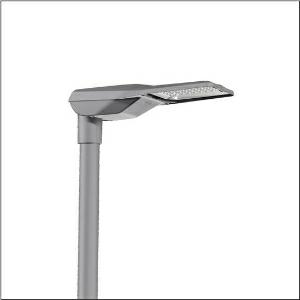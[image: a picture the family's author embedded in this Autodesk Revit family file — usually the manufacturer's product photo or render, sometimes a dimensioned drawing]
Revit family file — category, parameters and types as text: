
# Revit family: streetlight_sl_21_iq_mini___p0_8a_5xe2u31g08gb_20f9
name_source: partatom
category: Lighting Fixtures
units: mm (PartAtom-declared; Revit-internal decimal feet)

## family parameters
Cut with Voids When Loaded = No
Host = Face
Light Source = No
Part Type = Normal
Room Calculation Point = No
Round Connector Dimension = Use Diameter
Shared = No

## types (1)
- --- (1 x LED, 5730 lm, 37.1 W, 3000K)
    Apparent Load = 37 VA
    CIE Flux Codes = 33 69 96 100 100
    Color Rendering = 70
    Color Temperature = 3000K
    Default Elevation = 1800 mm
    Description = Streetlight SL 21 iQ mini, mast luminaire, primary light control with lens, of PMMA, primary optical cover: cover, of toughened safety glass, transparent, light distribution: P0.8a, light emission: direct distribution, primary light characteristic: asymmetric, installation type: post-top, side-entry, LED, High Power LED, rated luminous flux: 5.730lm, luminous efficacy: 154lm/W, light colour: 730, colour temperature: 3000K, control gear: iQ Street-Remote, control: pre-setting: linear dimming characteristic, Street-Remote, Auto-Match, Temp-Guard, Lumen-Switch, Night-Set, Smart-Wire, Light-Fading, Desk-Remote (wireless, voltage-free reading and setting of iQ features in the workshop via application-optimized NFC function/RFID function), optimised constant luminous flux control (CLO 2.0), mains connection: 220..240V, AC, 50/60Hz, start of lifetime: 37W, end of service life: 39W, reduction: 18W, luminaire housing, of diecast aluminium, powder-coated, SITECO metallic grey (DB 702S), corrosivity category C5 high according to DIN EN ISO 12944, please order mast flange separately, inclination adjustable: 0°, 5°, 10°, 15°, sealing non-destructively replaceable, multi-level sealing system, length: 628mm, width: 235mm, height: 110mm, mast flange for spigot size: 42mm (side-entry): 5XC10008XM4, 60/48mm (side-entry/post-top): 5XC10108XM2, 76/60mm (side-entry/post-top): 5XC10108XM1, mounting height: 4..8m, protection rating (complete): IP66, insulation class (complete): insulation class II (safety insulation), certification: CE, ENEC, ENEC+, VDE, impact resistance: IK10, permissible operating ambient temperature for outdoor applications: -40..+50°C, standard-compliant lighting for roads and squares, packaging unit: 1 piece

Light Distribution: P0.8a
    Height = 110 mm
    Lamp = 1 x LED
    Lamp Light Flux = 5730 lm
    Lamp Power = 37.1 W
    Lamp count = 1
    Length = 625 mm
    Luminous efficacy = 154 lm/W
    Manufacturer = Siteco
    ModVariant = No
    Model = 5XE2U31G08GB
    Number of Poles = 1
    OnlyDefault = Yes
    Power Factor = 1
    Product Name = Streetlight SL 21 iQ mini | P0.8a
    Product group = mast luminaire | pylon top
    ProductGroupID = 6100
    Protection Class = Protection class II
    Protection Degree = IP 66
    RLX_Detail_Level = 1
    RLX_Emergency_Light_Flux = 0 lm
    RLX_Emergency_Type = 0
    RLX_Emergency_Type_DB = No
    RlxData = <blob elided: 91865 chars, md5=2855600a>
    Socket = socket
    Standby Power = 0 W
    System Light Flux = 5730 lm
    System Power = 37 W
    Type Comments = factory setting: luminous flux: 100 % | dim-lin: 254 | 385 mA
    Type Image = l_1003519.jpg
    URL = http://relux.com
    VarID = @adj_080441
    Voltage = 0 V
    Weight = 0.00 kg
    Width = 234 mm

## geometry (parser evidence)
native form markers: Blend x4, Sweep x12
no freeform markers — native parametric forms only
